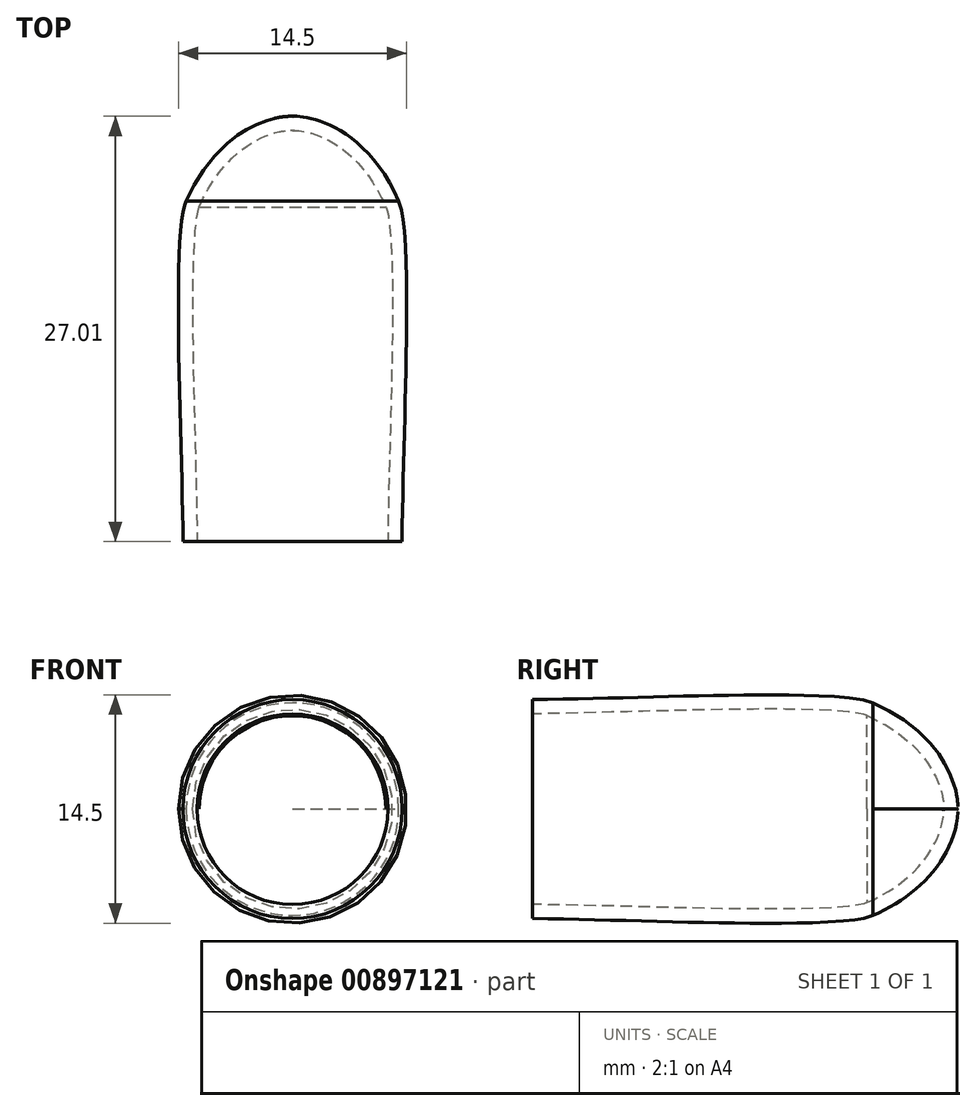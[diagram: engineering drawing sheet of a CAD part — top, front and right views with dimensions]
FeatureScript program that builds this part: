
annotation { "Feature Type Name" : "Feature", "Feature Type Description" : "" }
export const myFeature = defineFeature(function(context is Context, id is Id, definition is map)
    precondition{}
    {
        {
            var Q0;
            Q0=qCreatedBy(makeId("Top.planeOp"),FACE);
            var sketch = newSketch(context, id + "F0", { "sketchPlane" : qUnion([Q0])});
            skLineSegment(sketch, "E0", {"start": v(-1.17, 44.96) * mm, "end": v(-1.17, 17.96) * mm});
            skFitSpline(sketch, "E1", {"points": [v(-1.17, 44.96) * mm, v(5.58, 39.59) * mm], "startDerivative": vector(2.58, 0.26) * mm, "endDerivative": vector(6.5, -14.72) * mm});
            skFitSpline(sketch, "E2", {"points": [v(5.58, 39.59) * mm, v(5.79, 17.96) * mm], "startDerivative": vector(2.88, -5.35) * mm, "endDerivative": vector(-0.15, -18.95) * mm});
            skLineSegment(sketch, "E3", {"start": v(-1.17, 17.96) * mm, "end": v(5.79, 17.96) * mm});
            skSolve(sketch);
        }
        {
            var Q0;
            Q0=makeQuery(id+"F0.imprint","IMPRINT",FACE,{"disambiguationData":[TD([[makeQuery(id+"F0.imprint","IMPRINT",EDGE,{"derivedFrom":sQuery(id+"F0.wireOp",EDGE,"E0")}),1.0]])]});
            var Q1;
            Q1=sQuery(id+"F0.wireOp",EDGE,"E0");
            revolve(context, id + "F1", {"surfaceOperationType" : NewSurfaceOperationType.NEW, "entities" : qUnion([Q0]), "axis" : qUnion([Q1]), "revolveType" : RevolveType.FULL});
        }
        {
            var Q0;
            Q0=makeQuery(id+"F1.opRevolve","SWEPT_FACE",FACE,{"disambiguationData":[OSD([sQuery(id+"F0.wireOp",EDGE,"E3")])]});
            shell(context, id + "F2", {"entities" : qUnion([Q0]), "thickness" : .9 * mm});
        }
    });
